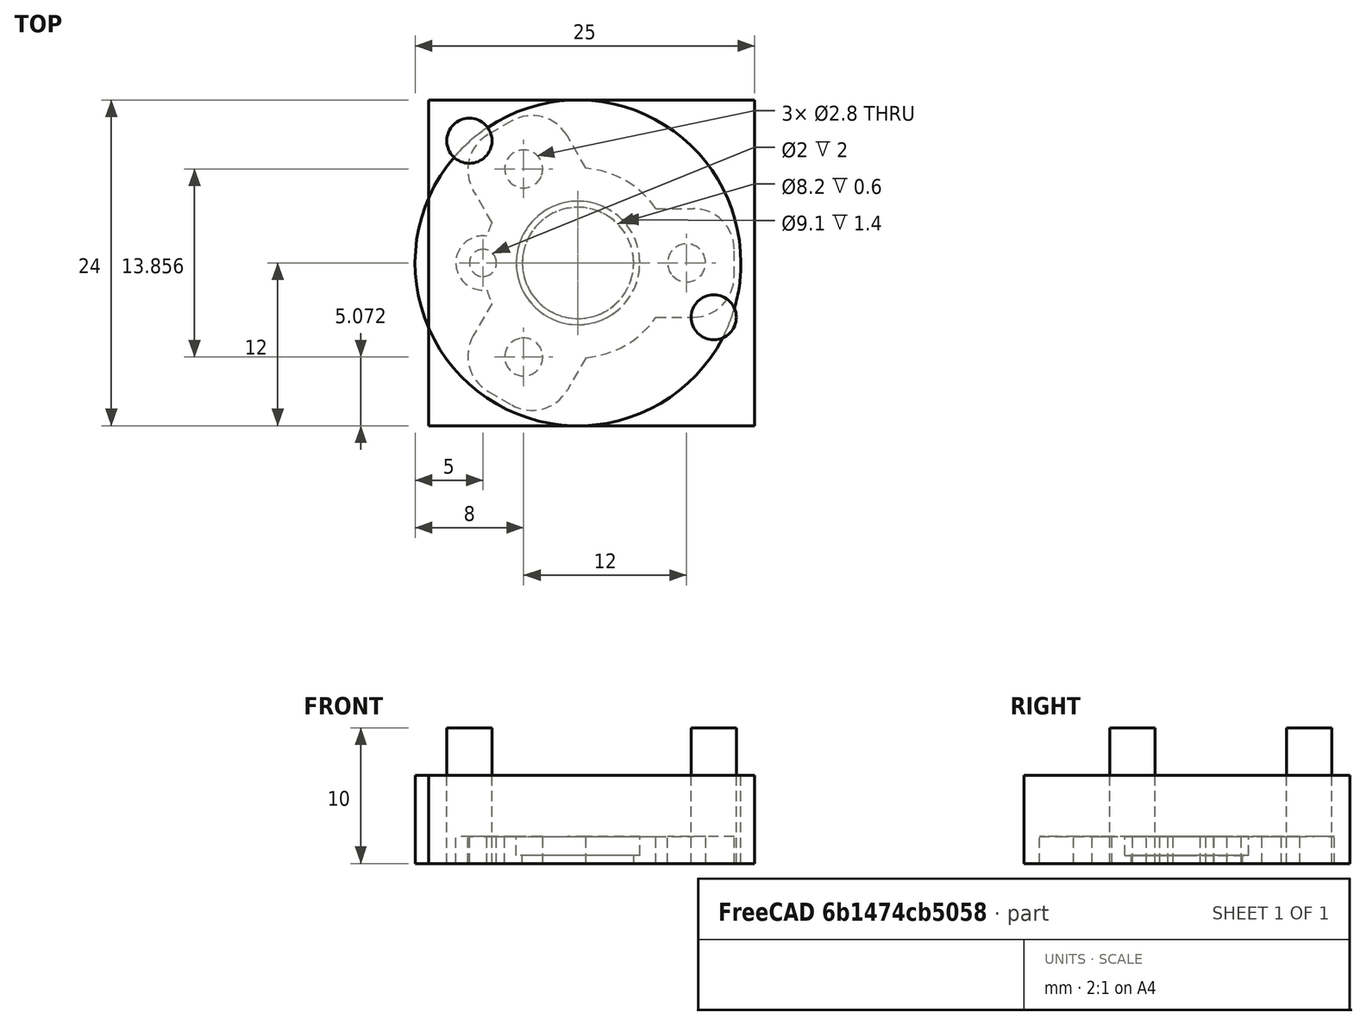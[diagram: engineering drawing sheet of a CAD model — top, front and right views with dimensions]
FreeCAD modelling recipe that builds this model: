
FCSTD DOCUMENT  (FreeCAD 0.18R16033 (Git))
Label: test_2
License: All rights reserved
LicenseURL: http://en.wikipedia.org/wiki/All_rights_reserved
objects: Part::Cylinder×15, Part::FeaturePython×4, Part::MultiFuse×4, Part::Box×3, Part::Fillet×2, Part::Cut×2
note: 30 computed .brp shape members not serialized (recipe doc carries the construction recipe); baked Part::Feature solids carry a one-line shape summary decoded from their .brp

FEATURE [Part::Cylinder] Cylinder023  label="MountPlateBody"
  Angle = 360
  AttacherType = Attacher::AttachEngine3D
  Height = 2
  Radius = 7
FEATURE [Part::Cylinder] Cylinder024  label="Cylinder016"
  Angle = 360
  AttacherType = Attacher::AttachEngine3D
  Height = 10
  Placement = pos=(8,0,0) rot=(0,0,1;0rad)
  Radius = 1.4
FEATURE [Part::FeaturePython] Array  # Draft array (typed FeaturePython)
  Angle = 360
  ArrayType = 1
  Axis = (0,0,1)
  Base = -> Cylinder024
  Center = (0,0,0)
  Fuse = false
  IntervalAxis = (0,0,0)
  IntervalX = (1,0,0)
  IntervalY = (0,1,0)
  IntervalZ = (0,0,1)
  NumberPolar = 3
  NumberX = 2
  NumberY = 2
  NumberZ = 1
FEATURE [Part::Cylinder] Cylinder026  label="MountPlateInnerHole"
  Angle = 360
  AttacherType = Attacher::AttachEngine3D
  Height = 10
  Radius = 4.1
FEATURE [Part::Cylinder] Cylinder027  label="MountPlateLip"
  Angle = 360
  AttacherType = Attacher::AttachEngine3D
  Height = 10
  Placement = pos=(0,0,0.6) rot=(0,0,1;0rad)
  Radius = 4.55
FEATURE [Part::Box] Box001  label="Cube001"
  AttacherType = Attacher::AttachEngine3D
  Height = 2
  Length = 9
  Placement = pos=(2.5,-4,0) rot=(0,0,1;0rad)
  Width = 8
FEATURE [Part::Fillet] Fillet
  Base = -> Box001
  Edges = 2 edges r=3: [Edge5,Edge7]
FEATURE [Part::FeaturePython] Array001  # Draft array (typed FeaturePython)
  Angle = 360
  ArrayType = 1
  Axis = (0,0,1)
  Base = -> Fillet
  Center = (0,0,0)
  Fuse = false
  IntervalAxis = (0,0,0)
  IntervalX = (1,0,0)
  IntervalY = (0,1,0)
  IntervalZ = (0,0,1)
  NumberPolar = 3
  NumberX = 2
  NumberY = 2
  NumberZ = 1
FEATURE [Part::Cylinder] Cylinder033  label="Cylinder018"
  Angle = 360
  AttacherType = Attacher::AttachEngine3D
  Height = 10
  Placement = pos=(-7,0,0) rot=(0,0,1;0rad)
  Radius = 1
FEATURE [Part::Cylinder] Cylinder034  label="Cylinder019"
  Angle = 360
  AttacherType = Attacher::AttachEngine3D
  Height = 2
  Placement = pos=(-7,0,0) rot=(0,0,1;0rad)
  Radius = 2
FEATURE [Part::MultiFuse] Fusion008
  Shapes = -> [Cylinder034,Array001,Cylinder023]
FEATURE [Part::MultiFuse] Fusion009
  Shapes = -> [Array,Cylinder027,Cylinder026,Cylinder033]
FEATURE [Part::Cut] Cut010
  Base = -> Fusion008
  Tool = -> Fusion009
FEATURE [Part::Cylinder] Cylinder044  label="Cylinder026"
  Angle = 360
  AttacherType = Attacher::AttachEngine3D
  Height = 6.5
  Radius = 12
FEATURE [Part::Cylinder] Cylinder  label="Sprue"
  Angle = 360
  AttacherType = Attacher::AttachEngine3D
  Height = 10
  Placement = pos=(10,-4,0) rot=(0,0,1;0rad)
  Radius = 1.66
FEATURE [Part::Box] Box  label="Cube"
  AttacherType = Attacher::AttachEngine3D
  Height = 6.5
  Length = 24
  Placement = pos=(-11,-12,0) rot=(0,0,1;0rad)
  Width = 24
FEATURE [Part::Cylinder] Cylinder045  label="Sprue001"
  Angle = 360
  AttacherType = Attacher::AttachEngine3D
  Height = 10
  Placement = pos=(-8,9,0) rot=(0,0,1;0rad)
  Radius = 1.66
FEATURE [Part::Cylinder] Cylinder046  label="Cylinder027"
  Angle = 360
  AttacherType = Attacher::AttachEngine3D
  Height = 10
  Placement = pos=(-7,0,0) rot=(0,0,1;0rad)
  Radius = 1
FEATURE [Part::Cylinder] Cylinder047  label="Cylinder028"
  Angle = 360
  AttacherType = Attacher::AttachEngine3D
  Height = 10
  Placement = pos=(8,0,0) rot=(0,0,1;0rad)
  Radius = 1.4
FEATURE [Part::FeaturePython] Array002  # Draft array (typed FeaturePython)
  Angle = 360
  ArrayType = 1
  Axis = (0,0,1)
  Base = -> Cylinder047
  Center = (0,0,0)
  Fuse = false
  IntervalAxis = (0,0,0)
  IntervalX = (1,0,0)
  IntervalY = (0,1,0)
  IntervalZ = (0,0,1)
  NumberPolar = 3
  NumberX = 2
  NumberY = 2
  NumberZ = 1
FEATURE [Part::Cylinder] Cylinder048  label="MountPlateInnerHole001"
  Angle = 360
  AttacherType = Attacher::AttachEngine3D
  Height = 10
  Radius = 4.1
FEATURE [Part::Cylinder] Cylinder049  label="MountPlateLip001"
  Angle = 360
  AttacherType = Attacher::AttachEngine3D
  Height = 10
  Placement = pos=(0,0,0.6) rot=(0,0,1;0rad)
  Radius = 4.55
FEATURE [Part::MultiFuse] Fusion011
  Shapes = -> [Array002,Cylinder049,Cylinder048,Cylinder046]
FEATURE [Part::Cylinder] Cylinder050  label="MountPlateBody001"
  Angle = 360
  AttacherType = Attacher::AttachEngine3D
  Height = 2
  Radius = 7
FEATURE [Part::Cylinder] Cylinder051  label="Cylinder029"
  Angle = 360
  AttacherType = Attacher::AttachEngine3D
  Height = 2
  Placement = pos=(-7,0,0) rot=(0,0,1;0rad)
  Radius = 2
FEATURE [Part::Box] Box002  label="Cube002"
  AttacherType = Attacher::AttachEngine3D
  Height = 2
  Length = 9
  Placement = pos=(2.5,-4,0) rot=(0,0,1;0rad)
  Width = 8
FEATURE [Part::Fillet] Fillet001
  Base = -> Box002
  Edges = 2 edges r=3: [Edge5,Edge7]
FEATURE [Part::FeaturePython] Array003  # Draft array (typed FeaturePython)
  Angle = 360
  ArrayType = 1
  Axis = (0,0,1)
  Base = -> Fillet001
  Center = (0,0,0)
  Fuse = false
  IntervalAxis = (0,0,0)
  IntervalX = (1,0,0)
  IntervalY = (0,1,0)
  IntervalZ = (0,0,1)
  NumberPolar = 3
  NumberX = 2
  NumberY = 2
  NumberZ = 1
FEATURE [Part::MultiFuse] Fusion010
  Shapes = -> [Cylinder051,Array003,Cylinder050]
FEATURE [Part::Cut] Cut011
  Base = -> Fusion010
  Tool = -> Fusion011
